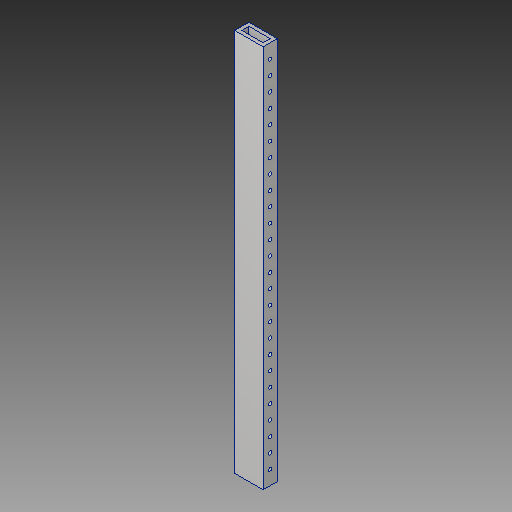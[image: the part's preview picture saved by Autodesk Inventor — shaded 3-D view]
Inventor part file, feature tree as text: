
AUTODESK INVENTOR PART (.ipt)
format: ipt  version: 2017 (Build 210142000, 142)  size: 161,792 bytes
history: native  units: in
note: dims shown in document units (in); Inventor stores cm internally (conversion verified against a paired STEP export)
features: extrude x3, sketch x3, pattern_linear x1
ambient origin geometry x8: Origin, YZ Plane, XZ Plane, XY Plane, X Axis, Y Axis, Z Axis, Center Point
bodies: Solid1 (feature_tree)
feature tree (7):
  extrude  "Extrusion1"  Depth=27.0in
  extrude  "Extrusion2"  Depth=0.25in
  extrude  "Extrusion3"  Depth=0.25in
  pattern_linear  "Rectangular Pattern1"  Spacing1=1.0in  [1 undecoded]
  sketch  "Sketch1"  dims[d0=2.0in d1=27.0in]
  sketch  "Sketch2"  dims[d2=1.0in d3=0.0in d4=0.25in]
  sketch  "Sketch3"  dims[d5=1.0in d6=0.0in d7=0.25in d8=1.0in d9=1.0in d10=0.0in d11=10.2362in d13=1.0in]
note: 1 required parameter value undecoded (feature->parameter linkage not recoverable at this tier; creation-order binding heuristic only, values carry confidence <= 0.55)
